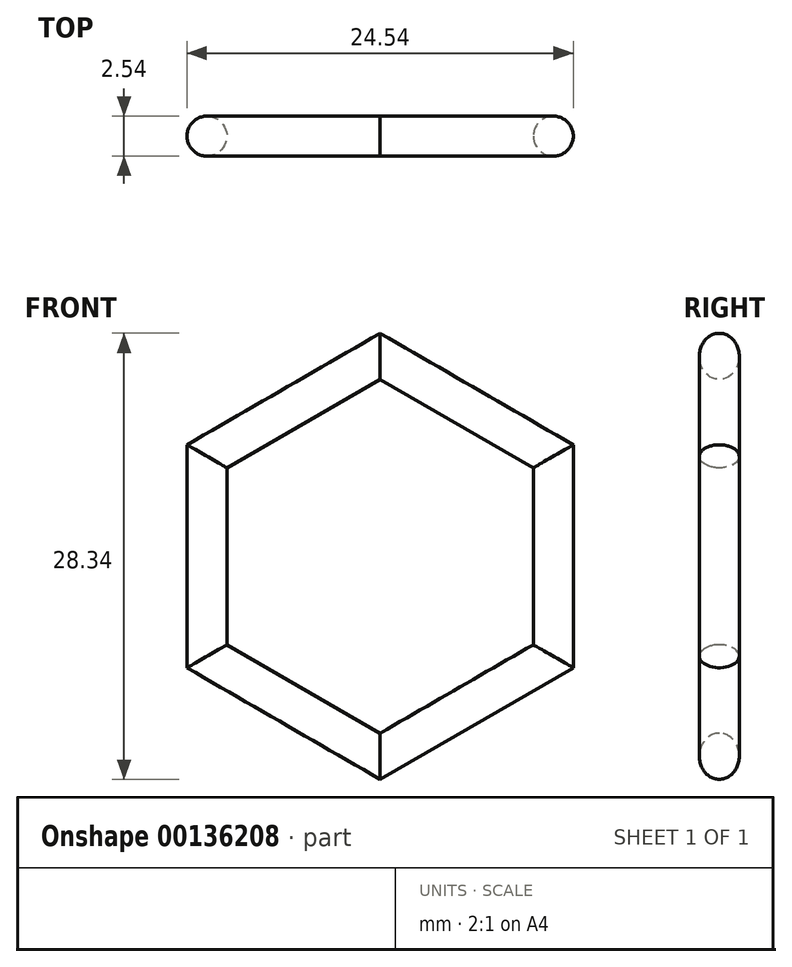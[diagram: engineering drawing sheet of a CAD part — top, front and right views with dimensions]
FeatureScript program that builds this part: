
annotation { "Feature Type Name" : "Feature", "Feature Type Description" : "" }
export const myFeature = defineFeature(function(context is Context, id is Id, definition is map)
    precondition{}
    {
        {
            var Q0;
            Q0=qCreatedBy(makeId("Front.planeOp"),FACE);
            var sketch = newSketch(context, id + "F0", { "sketchPlane" : qUnion([Q0])});
            skCircle(sketch, "E0.cCircle", {"center": v(0, 0) * mm, "radius": 11 * mm, "construction": true});
            skLineSegment(sketch, "E0.0", {"start": v(11, 6.35) * mm, "end": v(11, -6.35) * mm});
            skLineSegment(sketch, "E0.1", {"start": v(11, -6.35) * mm, "end": v(0, -12.7) * mm});
            skLineSegment(sketch, "E0.2", {"start": v(0, -12.7) * mm, "end": v(-11, -6.35) * mm});
            skLineSegment(sketch, "E0.3", {"start": v(-11, -6.35) * mm, "end": v(-11, 6.35) * mm});
            skLineSegment(sketch, "E0.4", {"start": v(-11, 6.35) * mm, "end": v(0, 12.7) * mm});
            skLineSegment(sketch, "E0.5", {"start": v(0, 12.7) * mm, "end": v(11, 6.35) * mm});
            skPoint(sketch, "E0.0.midPoint", {"position": v(11, 0) * mm});
            skSolve(sketch);
        }
        {
            var Q0;
            Q0=qCreatedBy(makeId("Top.planeOp"),FACE);
            var sketch = newSketch(context, id + "F1", { "sketchPlane" : qUnion([Q0])});
            skCircle(sketch, "E1", {"center": v(11, 0) * mm, "radius": 1.27 * mm});
            skSolve(sketch);
        }
        {
            var Q0;
            Q0=makeQuery(id+"F1.imprint","IMPRINT",FACE,{"disambiguationData":[TD([[makeQuery(id+"F1.imprint","IMPRINT",EDGE,{"derivedFrom":sQuery(id+"F1.wireOp",EDGE,"E1")}),1.0]])]});
            var Q1;
            Q1=sQuery(id+"F0.wireOp",EDGE,"E0.0");
            var Q2;
            Q2=sQuery(id+"F0.wireOp",EDGE,"E0.5");
            var Q3;
            Q3=sQuery(id+"F0.wireOp",EDGE,"E0.4");
            var Q4;
            Q4=sQuery(id+"F0.wireOp",EDGE,"E0.3");
            var Q5;
            Q5=sQuery(id+"F0.wireOp",EDGE,"E0.2");
            var Q6;
            Q6=sQuery(id+"F0.wireOp",EDGE,"E0.1");
            sweep(context, id + "F2", {"profiles" : qUnion([Q0]), "path" : qUnion([Q1, Q2, Q3, Q4, Q5, Q6])});
        }
    });
